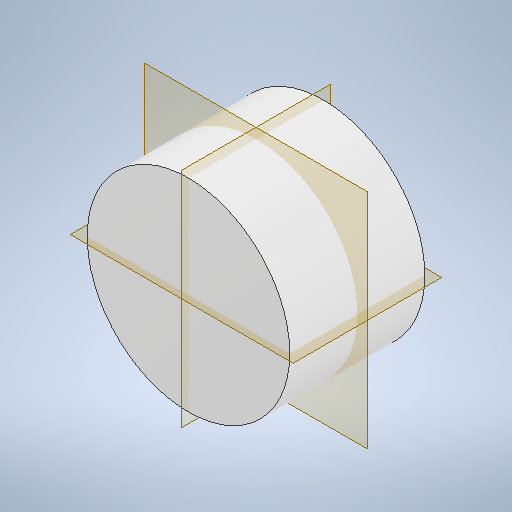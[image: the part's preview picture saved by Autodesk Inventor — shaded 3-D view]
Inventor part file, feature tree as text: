
AUTODESK INVENTOR PART (.ipt)
format: ipt  version: 2025.2 (Build 292293000, 293)  size: 207,872 bytes
history: native  units: mm
features: other x1, extrude x1, sketch x1
ambient origin geometry x8: Origin, YZ Plane, XZ Plane, XY Plane, X Axis, Y Axis, Z Axis, Center Point
bodies: Body1 (feature_tree)
feature tree (3):
  other  "Sólido1"
  extrude  "Extrusão1"  Depth=10.0mm TaperAngle=0.0deg
  sketch  "Esboço1"  dims[d0=15.0mm d1=10.0mm d2=0.0mm]
